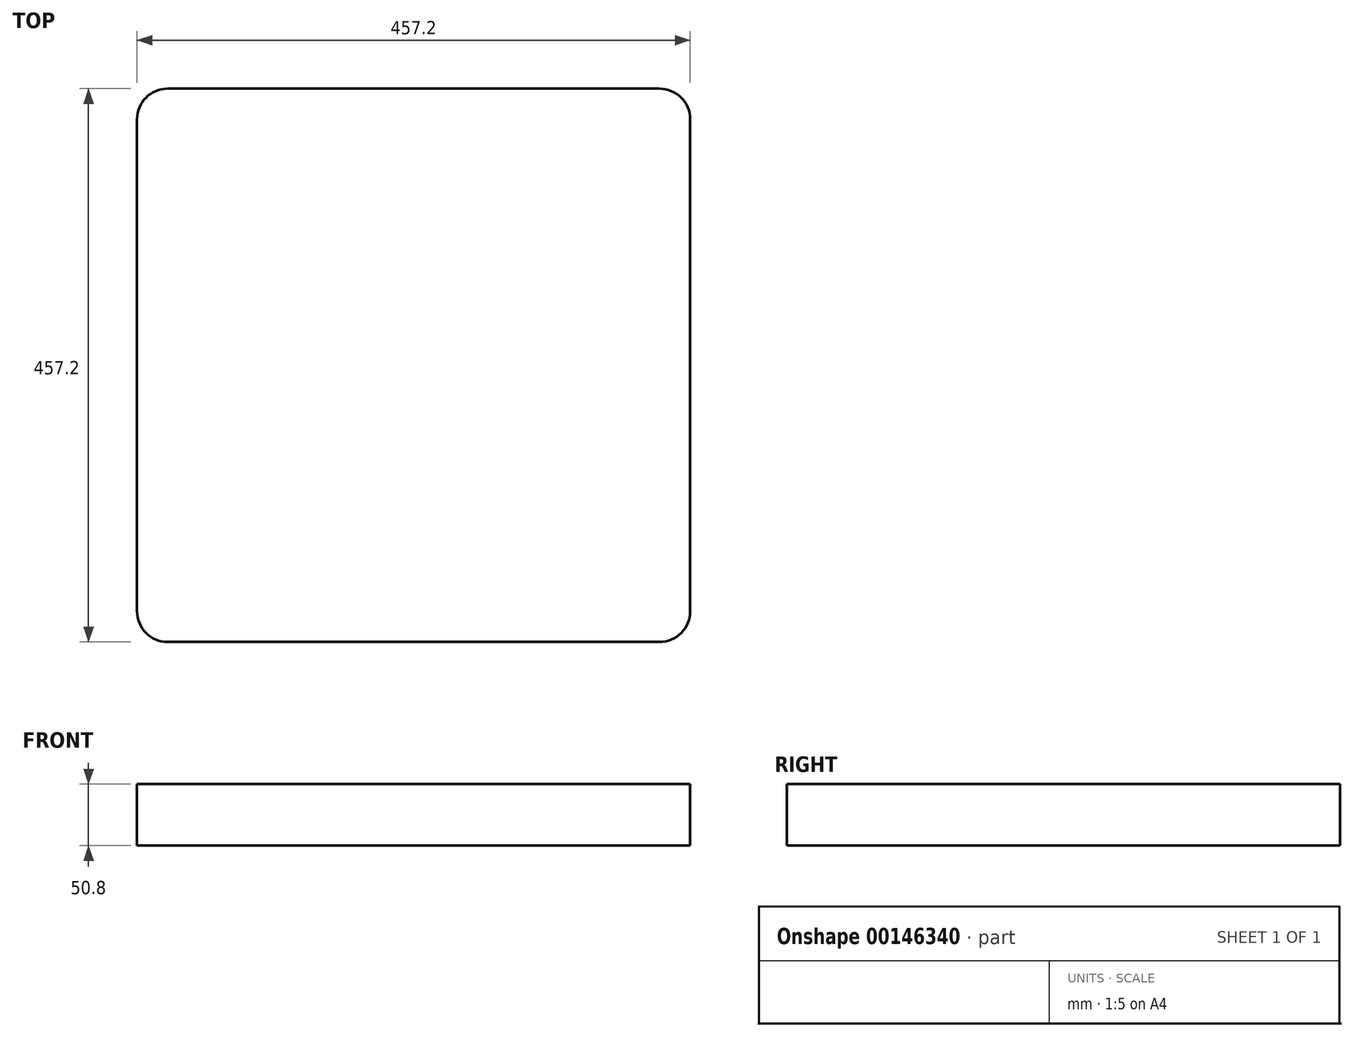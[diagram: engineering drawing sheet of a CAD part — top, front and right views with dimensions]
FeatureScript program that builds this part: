
annotation { "Feature Type Name" : "Feature", "Feature Type Description" : "" }
export const myFeature = defineFeature(function(context is Context, id is Id, definition is map)
    precondition{}
    {
        {
            var Q0;
            Q0=qCreatedBy(makeId("Top.planeOp"),FACE);
            var sketch = newSketch(context, id + "F0", { "sketchPlane" : qUnion([Q0])});
            skLineSegment(sketch, "E0.bottom", {"start": v(-226.06, 294.3) * mm, "end": v(231.14, 294.3) * mm});
            skLineSegment(sketch, "E0.top", {"start": v(-226.06, -162.9) * mm, "end": v(231.14, -162.9) * mm});
            skLineSegment(sketch, "E0.left", {"start": v(-226.06, 294.3) * mm, "end": v(-226.06, -162.9) * mm});
            skLineSegment(sketch, "E0.right", {"start": v(231.14, 294.3) * mm, "end": v(231.14, -162.9) * mm});
            skSolve(sketch);
        }
        {
            var Q0;
            Q0=makeQuery(id+"F0.imprint","IMPRINT",FACE,{"disambiguationData":[TD([[makeQuery(id+"F0.imprint","IMPRINT",EDGE,{"derivedFrom":sQuery(id+"F0.wireOp",EDGE,"E0.bottom")}),-1.0]])]});
            extrude(context, id + "F1", {"entities" : qUnion([Q0]), "depth" : 50.8 * mm});
        }
        {
            var Q0;
            Q0=makeQuery(id+"F1.opExtrude","SWEPT_EDGE",EDGE,{"disambiguationData":[OSD([sQuery(id+"F0.wireOp",EDGE,"E0.top"),sQuery(id+"F0.wireOp",EDGE,"E0.left")])]});
            var Q1;
            Q1=makeQuery(id+"F1.opExtrude","SWEPT_EDGE",EDGE,{"disambiguationData":[OSD([sQuery(id+"F0.wireOp",EDGE,"E0.bottom"),sQuery(id+"F0.wireOp",EDGE,"E0.left")])]});
            var Q2;
            Q2=makeQuery(id+"F1.opExtrude","SWEPT_EDGE",EDGE,{"disambiguationData":[OSD([sQuery(id+"F0.wireOp",EDGE,"E0.bottom"),sQuery(id+"F0.wireOp",EDGE,"E0.right")])]});
            var Q3;
            Q3=makeQuery(id+"F1.opExtrude","SWEPT_EDGE",EDGE,{"disambiguationData":[OSD([sQuery(id+"F0.wireOp",EDGE,"E0.top"),sQuery(id+"F0.wireOp",EDGE,"E0.right")])]});
            fillet(context, id + "F2", {"entities" : qUnion([Q0, Q1, Q2, Q3]), "radius" : 25.4 * mm, "tangentPropagation" : true, "allowEdgeOverflow" : false});
        }
    });
